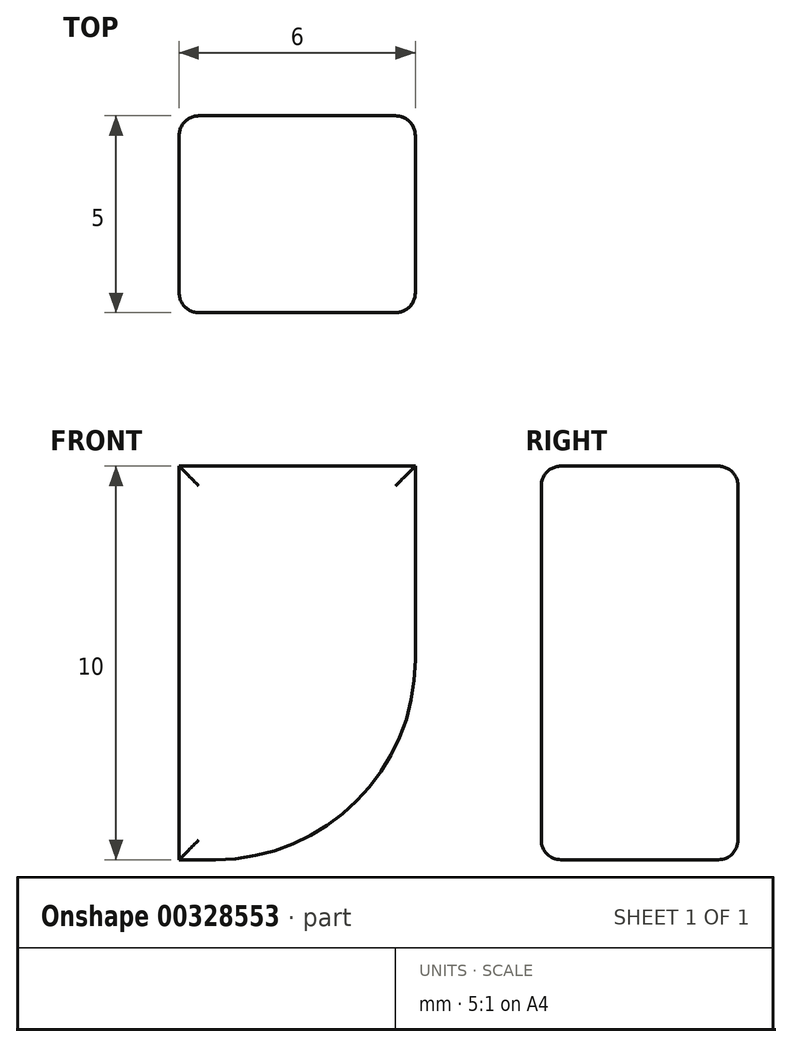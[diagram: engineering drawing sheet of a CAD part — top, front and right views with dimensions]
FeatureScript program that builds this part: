
annotation { "Feature Type Name" : "Feature", "Feature Type Description" : "" }
export const myFeature = defineFeature(function(context is Context, id is Id, definition is map)
    precondition{}
    {
        {
            var Q0;
            Q0=qCreatedBy(makeId("Top.planeOp"),FACE);
            var sketch = newSketch(context, id + "F0", { "sketchPlane" : qUnion([Q0])});
            skLineSegment(sketch, "E0.bottom", {"start": v(0, 0) * mm, "end": v(6, 0) * mm});
            skLineSegment(sketch, "E0.top", {"start": v(0, -5) * mm, "end": v(6, -5) * mm});
            skLineSegment(sketch, "E0.left", {"start": v(0, 0) * mm, "end": v(0, -5) * mm});
            skLineSegment(sketch, "E0.right", {"start": v(6, 0) * mm, "end": v(6, -5) * mm});
            skSolve(sketch);
        }
        {
            var Q0;
            Q0=makeQuery(id+"F0.imprint","IMPRINT",FACE,{"disambiguationData":[TD([[makeQuery(id+"F0.imprint","IMPRINT",EDGE,{"derivedFrom":sQuery(id+"F0.wireOp",EDGE,"E0.bottom")}),-1.0]])]});
            extrude(context, id + "F1", {"entities" : qUnion([Q0]), "depth" : 10 * mm});
        }
        {
            var Q0;
            Q0=makeQuery(id+"F1.opExtrude","SWEPT_EDGE",EDGE,{"disambiguationData":[OSD([sQuery(id+"F0.wireOp",EDGE,"E0.bottom"),sQuery(id+"F0.wireOp",EDGE,"E0.right")])]});
            var Q1;
            Q1=makeQuery(id+"F1.opExtrude","SWEPT_EDGE",EDGE,{"disambiguationData":[OSD([sQuery(id+"F0.wireOp",EDGE,"E0.bottom"),sQuery(id+"F0.wireOp",EDGE,"E0.left")])]});
            var Q2;
            Q2=makeQuery(id+"F1.opExtrude","CAP_EDGE",EDGE,{"disambiguationData":[OSD([sQuery(id+"F0.wireOp",EDGE,"E0.bottom")])],"isStart":true});
            var Q3;
            Q3=makeQuery(id+"F1.opExtrude","CAP_EDGE",EDGE,{"disambiguationData":[OSD([sQuery(id+"F0.wireOp",EDGE,"E0.bottom")])],"isStart":false});
            var Q4;
            Q4=makeQuery(id+"F1.opExtrude","CAP_EDGE",EDGE,{"disambiguationData":[OSD([sQuery(id+"F0.wireOp",EDGE,"E0.top")])],"isStart":true});
            var Q5;
            Q5=makeQuery(id+"F1.opExtrude","SWEPT_EDGE",EDGE,{"disambiguationData":[OSD([sQuery(id+"F0.wireOp",EDGE,"E0.top"),sQuery(id+"F0.wireOp",EDGE,"E0.left")])]});
            var Q6;
            Q6=makeQuery(id+"F1.opExtrude","SWEPT_EDGE",EDGE,{"disambiguationData":[OSD([sQuery(id+"F0.wireOp",EDGE,"E0.top"),sQuery(id+"F0.wireOp",EDGE,"E0.right")])]});
            var Q7;
            Q7=makeQuery(id+"F1.opExtrude","CAP_EDGE",EDGE,{"disambiguationData":[OSD([sQuery(id+"F0.wireOp",EDGE,"E0.top")])],"isStart":false});
            fillet(context, id + "F2", {"entities" : qUnion([Q0, Q1, Q2, Q3, Q4, Q5, Q6, Q7]), "radius" : 0.5 * mm, "tangentPropagation" : true, "allowEdgeOverflow" : false});
        }
        {
            var Q0;
            Q0=makeQuery(id+"F1.opExtrude","CAP_EDGE",EDGE,{"disambiguationData":[OSD([sQuery(id+"F0.wireOp",EDGE,"E0.right")])],"isStart":true});
            fillet(context, id + "F3", {"entities" : qUnion([Q0]), "radius" : 5.08 * mm, "tangentPropagation" : true, "allowEdgeOverflow" : false});
        }
    });
